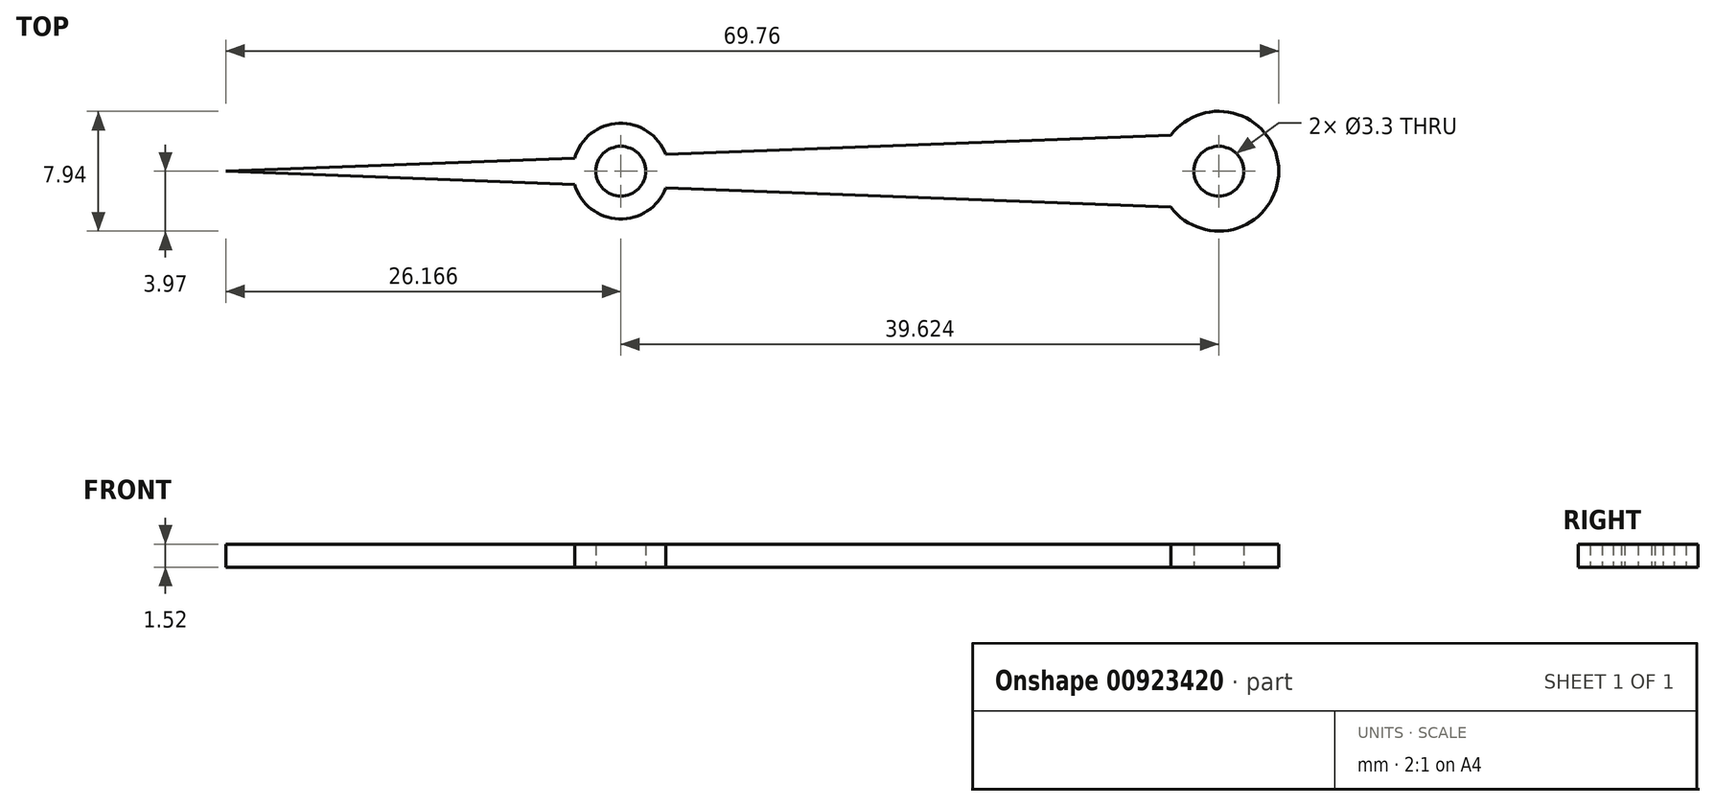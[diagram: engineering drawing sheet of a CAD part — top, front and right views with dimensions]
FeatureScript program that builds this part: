
annotation { "Feature Type Name" : "Feature", "Feature Type Description" : "" }
export const myFeature = defineFeature(function(context is Context, id is Id, definition is map)
    precondition{}
    {
        {
            var Q0;
            Q0=qCreatedBy(makeId("Top.planeOp"),FACE);
            var sketch = newSketch(context, id + "F0", { "sketchPlane" : qUnion([Q0])});
            skCircle(sketch, "E0", {"center": v(0, 0) * mm, "radius": 1.65 * mm});
            skCircle(sketch, "E1", {"center": v(-39.62, 0) * mm, "radius": 1.65 * mm});
            skArc(sketch, "E2", {"start": v(-3.18, -2.38) * mm, "mid": v(3.97, 0) * mm, "end": v(-3.17, 2.38) * mm});
            skArc(sketch, "E3", {"start": v(-36.65, 1.1) * mm, "mid": v(-39.74, 3.17) * mm, "end": v(-42.67, 0.88) * mm});
            skArc(sketch, "E4", {"start": v(-42.67, -0.88) * mm, "mid": v(-39.74, -3.17) * mm, "end": v(-36.65, -1.1) * mm});
            skLineSegment(sketch, "E5", {"start": v(-42.67, 0.88) * mm, "end": v(-65.79, 0) * mm});
            skLineSegment(sketch, "E6", {"start": v(-42.67, -0.88) * mm, "end": v(-65.79, 0) * mm});
            skLineSegment(sketch, "E7", {"start": v(-36.65, 1.1) * mm, "end": v(-3.17, 2.38) * mm});
            skLineSegment(sketch, "E8", {"start": v(-3.17, -2.38) * mm, "end": v(-36.65, -1.1) * mm});
            skSolve(sketch);
        }
        {
            var Q0;
            Q0 = qSketchRegion(id + "F0", true);
            extrude(context, id + "F1", {"entities" : qUnion([Q0]), "depth" : 1.52 * mm, "offsetDistance" : 25.4 * mm});
        }
    });
